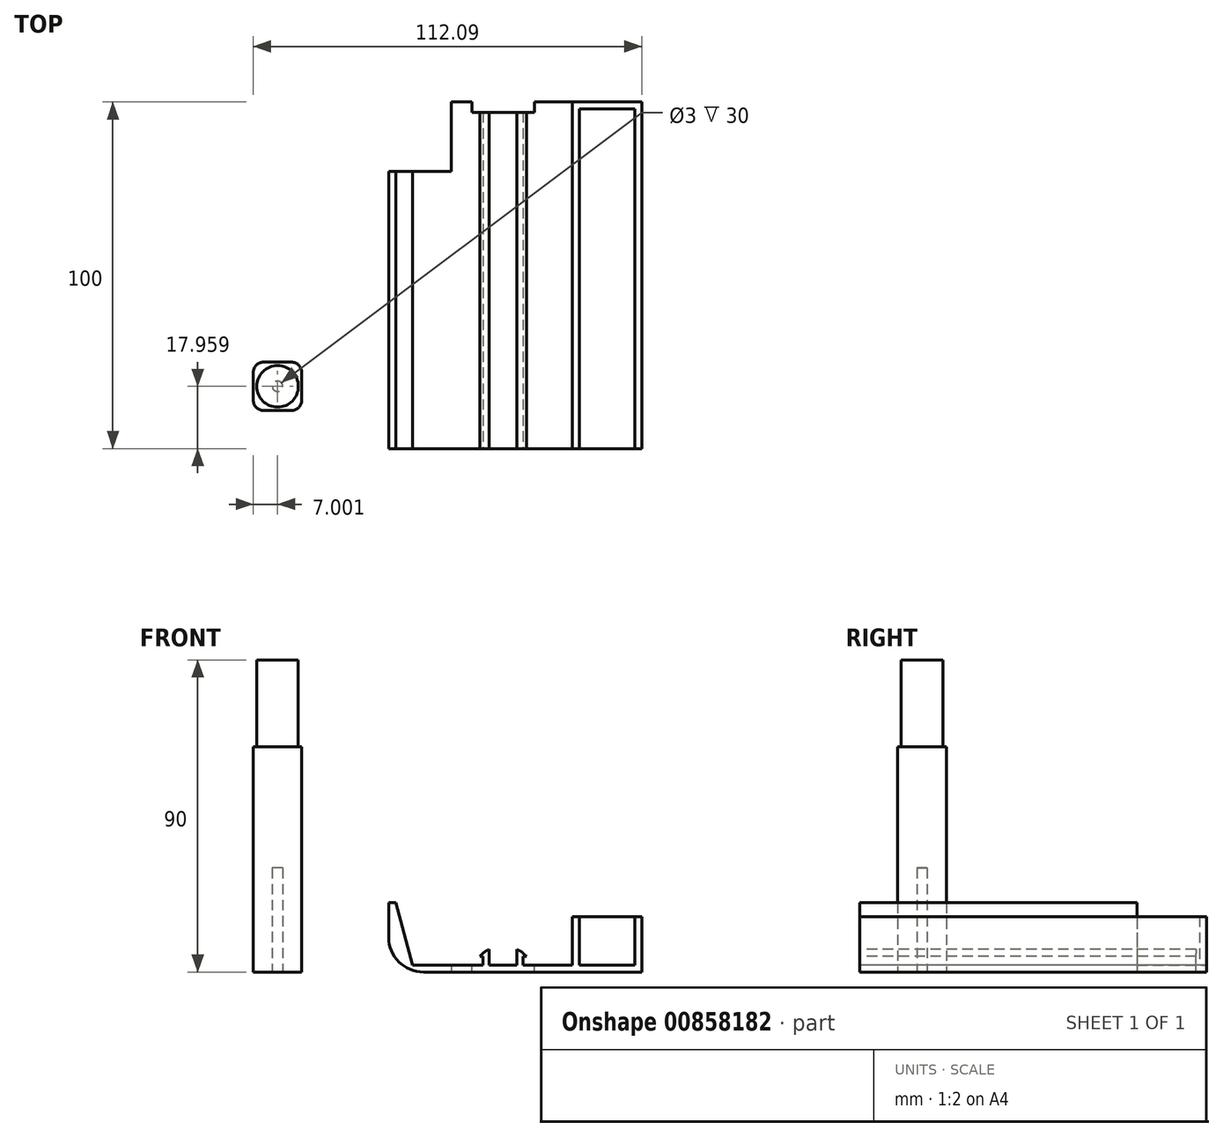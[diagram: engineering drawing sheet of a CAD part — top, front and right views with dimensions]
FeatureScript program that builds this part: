
annotation { "Feature Type Name" : "Feature", "Feature Type Description" : "" }
export const myFeature = defineFeature(function(context is Context, id is Id, definition is map)
    precondition{}
    {
        {
            var Q0;
            Q0=qCreatedBy(makeId("Top.planeOp"),FACE);
            var sketch = newSketch(context, id + "F0", { "sketchPlane" : qUnion([Q0])});
            skLineSegment(sketch, "E0.bottom", {"start": v(0, 0) * mm, "end": v(55, 0) * mm});
            skLineSegment(sketch, "E0.top", {"start": v(0, 100) * mm, "end": v(55, 100) * mm});
            skLineSegment(sketch, "E0.left", {"start": v(0, 0) * mm, "end": v(0, 100) * mm});
            skLineSegment(sketch, "E0.right", {"start": v(55, 0) * mm, "end": v(55, 100) * mm});
            skSolve(sketch);
        }
        {
            var Q0;
            Q0 = qSketchRegion(id + "F0", true);
            var Q1;
            Q1=makeQuery(id+"F0.imprint","IMPRINT",FACE,{"disambiguationData":[TD([[makeQuery(id+"F0.imprint","IMPRINT",EDGE,{"derivedFrom":sQuery(id+"F0.wireOp",EDGE,"E0.bottom")}),1.0]])]});
            extrude(context, id + "F1", {"entities" : qUnion([Q0, Q1]), "depth" : 2 * mm, "offsetDistance" : 25 * mm});
        }
        {
            var Q0;
            Q0=makeQuery(id+"F1.opExtrude","CAP_FACE",FACE,{"disambiguationData":[OSD([sQuery(id+"F0.wireOp",EDGE,"E0.bottom"),sQuery(id+"F0.wireOp",EDGE,"E0.top"),sQuery(id+"F0.wireOp",EDGE,"E0.left"),sQuery(id+"F0.wireOp",EDGE,"E0.right")])],"isStart":false});
            var sketch = newSketch(context, id + "F2", { "sketchPlane" : qUnion([Q0])});
            skLineSegment(sketch, "E1.bottom", {"start": v(55, 100) * mm, "end": v(53, 100) * mm});
            skLineSegment(sketch, "E1.top", {"start": v(55, 0) * mm, "end": v(53, 0) * mm});
            skLineSegment(sketch, "E1.left", {"start": v(55, 100) * mm, "end": v(55, 0) * mm});
            skLineSegment(sketch, "E1.right", {"start": v(53, 100) * mm, "end": v(53, 0) * mm});
            skLineSegment(sketch, "E2.bottom", {"start": v(35, 100) * mm, "end": v(37, 100) * mm});
            skLineSegment(sketch, "E2.top", {"start": v(35, 0) * mm, "end": v(37, 0) * mm});
            skLineSegment(sketch, "E2.left", {"start": v(35, 100) * mm, "end": v(35, 0) * mm});
            skLineSegment(sketch, "E2.right", {"start": v(37, 100) * mm, "end": v(37, 0) * mm});
            skLineSegment(sketch, "E3.bottom", {"start": v(37, 100) * mm, "end": v(53, 100) * mm});
            skLineSegment(sketch, "E3.top", {"start": v(37, 98) * mm, "end": v(53, 98) * mm});
            skLineSegment(sketch, "E3.left", {"start": v(37, 100) * mm, "end": v(37, 98) * mm});
            skLineSegment(sketch, "E3.right", {"start": v(53, 100) * mm, "end": v(53, 98) * mm});
            skSolve(sketch);
        }
        {
            var Q0;
            Q0=makeQuery(id+"F2.imprint","IMPRINT",FACE,{"disambiguationData":[TD([[makeQuery(id+"F2.imprint","IMPRINT",EDGE,{"derivedFrom":sQuery(id+"F2.wireOp",EDGE,"E2.bottom")}),-1.0]])]});
            var Q1;
            Q1=makeQuery(id+"F2.imprint","IMPRINT",FACE,{"disambiguationData":[TD([[makeQuery(id+"F2.imprint","IMPRINT",EDGE,{"derivedFrom":sQuery(id+"F2.wireOp",EDGE,"E1.bottom")}),-1.0]])]});
            var Q2;
            Q2=makeQuery(id+"F2.imprint","IMPRINT",FACE,{"disambiguationData":[TD([[makeQuery(id+"F2.imprint","IMPRINT",EDGE,{"derivedFrom":sQuery(id+"F2.wireOp",EDGE,"E3.bottom")}),-1.0]])]});
            extrude(context, id + "F3", {"entities" : qUnion([Q0, Q1, Q2]), "operationType" : NewBodyOperationType.ADD, "depth" : 14 * mm, "offsetDistance" : 25 * mm});
        }
        {
            var Q0;
            {var subQ0=sQuery(id+"F0.wireOp",EDGE,"E0.left");var subQ1=sQuery(id+"F0.wireOp",EDGE,"E0.top");var subQ2=sQuery(id+"F0.wireOp",EDGE,"E0.bottom");Q0=makeQuery(id+"F3.boolean.opBoolean","SPLIT",FACE,{"disambiguationData":[TD([makeQuery(id+"F1.opExtrude","SWEPT_FACE",FACE,{"disambiguationData":[OSD([subQ0])]})])],"derivedFrom":makeQuery(id+"F1.opExtrude","CAP_FACE",FACE,{"disambiguationData":[OSD([subQ2,subQ1,subQ0,sQuery(id+"F0.wireOp",EDGE,"E0.right")])],"isStart":false})});}
            var sketch = newSketch(context, id + "F4", { "sketchPlane" : qUnion([Q0])});
            skLineSegment(sketch, "E4.bottom", {"start": v(9.2, 100) * mm, "end": v(11, 100) * mm});
            skLineSegment(sketch, "E4.top", {"start": v(9.2, 0) * mm, "end": v(11, 0) * mm});
            skLineSegment(sketch, "E4.left", {"start": v(9.2, 100) * mm, "end": v(9.2, 0) * mm});
            skLineSegment(sketch, "E4.right", {"start": v(11, 100) * mm, "end": v(11, 0) * mm});
            skLineSegment(sketch, "E5.bottom", {"start": v(19, 100) * mm, "end": v(20.8, 100) * mm});
            skLineSegment(sketch, "E5.top", {"start": v(19, 0) * mm, "end": v(20.8, 0) * mm});
            skLineSegment(sketch, "E5.left", {"start": v(19, 100) * mm, "end": v(19, 0) * mm});
            skLineSegment(sketch, "E5.right", {"start": v(20.8, 100) * mm, "end": v(20.8, 0) * mm});
            skSolve(sketch);
        }
        {
            var Q0;
            Q0=makeQuery(id+"F4.imprint","IMPRINT",FACE,{"disambiguationData":[TD([[makeQuery(id+"F4.imprint","IMPRINT",EDGE,{"derivedFrom":sQuery(id+"F4.wireOp",EDGE,"E4.bottom")}),-1.0]])]});
            var Q1;
            Q1=makeQuery(id+"F4.imprint","IMPRINT",FACE,{"disambiguationData":[TD([[makeQuery(id+"F4.imprint","IMPRINT",EDGE,{"derivedFrom":sQuery(id+"F4.wireOp",EDGE,"E5.bottom")}),-1.0]])]});
            extrude(context, id + "F5", {"entities" : qUnion([Q0, Q1]), "operationType" : NewBodyOperationType.ADD, "depth" : 2.5 * mm, "offsetDistance" : 25 * mm});
        }
        {
            var Q0;
            Q0=makeQuery(id+"F5.opExtrude","CAP_FACE",FACE,{"disambiguationData":[OSD([sQuery(id+"F4.wireOp",EDGE,"E4.bottom"),sQuery(id+"F4.wireOp",EDGE,"E4.top"),sQuery(id+"F4.wireOp",EDGE,"E4.left"),sQuery(id+"F4.wireOp",EDGE,"E4.right")])],"isStart":false});
            var sketch = newSketch(context, id + "F6", { "sketchPlane" : qUnion([Q0])});
            skLineSegment(sketch, "E6.bottom", {"start": v(11, 0) * mm, "end": v(8.3, 0) * mm});
            skLineSegment(sketch, "E6.top", {"start": v(11, 100) * mm, "end": v(8.3, 100) * mm});
            skLineSegment(sketch, "E6.left", {"start": v(11, 0) * mm, "end": v(11, 100) * mm});
            skLineSegment(sketch, "E6.right", {"start": v(8.3, 0) * mm, "end": v(8.3, 100) * mm});
            skSolve(sketch);
        }
        {
            var Q0;
            Q0=makeQuery(id+"F5.opExtrude","CAP_FACE",FACE,{"disambiguationData":[OSD([sQuery(id+"F4.wireOp",EDGE,"E5.bottom"),sQuery(id+"F4.wireOp",EDGE,"E5.top"),sQuery(id+"F4.wireOp",EDGE,"E5.left"),sQuery(id+"F4.wireOp",EDGE,"E5.right")])],"isStart":false});
            var sketch = newSketch(context, id + "F7", { "sketchPlane" : qUnion([Q0])});
            skLineSegment(sketch, "E7.bottom", {"start": v(19, 100) * mm, "end": v(21.7, 100) * mm});
            skLineSegment(sketch, "E7.top", {"start": v(19, 0) * mm, "end": v(21.7, 0) * mm});
            skLineSegment(sketch, "E7.left", {"start": v(19, 100) * mm, "end": v(19, 0) * mm});
            skLineSegment(sketch, "E7.right", {"start": v(21.7, 100) * mm, "end": v(21.7, 0) * mm});
            skSolve(sketch);
        }
        {
            var Q0;
            {var subQ0=sQuery(id+"F7.wireOp",EDGE,"E7.left");Q0=makeQuery(id+"F7.imprint","IMPRINT",FACE,{"disambiguationData":[TD([[makeQuery(id+"F7.imprint","IMPRINT",EDGE,{"derivedFrom":subQ0}),1.0]])]});}
            var Q1;
            {var subQ2=sQuery(id+"F7.wireOp",EDGE,"E7.right");Q1=makeQuery(id+"F7.imprint","IMPRINT",FACE,{"disambiguationData":[TD([[makeQuery(id+"F7.imprint","IMPRINT",EDGE,{"derivedFrom":subQ2}),-1.0]])]});}
            var Q2;
            {var subQ2=sQuery(id+"F6.wireOp",EDGE,"E6.left");Q2=makeQuery(id+"F6.imprint","IMPRINT",FACE,{"disambiguationData":[TD([[makeQuery(id+"F6.imprint","IMPRINT",EDGE,{"derivedFrom":subQ2}),-1.0]])]});}
            var Q3;
            {var subQ2=sQuery(id+"F6.wireOp",EDGE,"E6.right");Q3=makeQuery(id+"F6.imprint","IMPRINT",FACE,{"disambiguationData":[TD([[makeQuery(id+"F6.imprint","IMPRINT",EDGE,{"derivedFrom":subQ2}),-1.0]])]});}
            extrude(context, id + "F8", {"entities" : qUnion([Q0, Q1, Q2, Q3]), "operationType" : NewBodyOperationType.ADD, "depth" : 2 * mm, "offsetDistance" : 25 * mm});
        }
        {
            var Q0;
            Q0=makeQuery(id+"F8.opExtrude","CAP_EDGE",EDGE,{"disambiguationData":[OSD([sQuery(id+"F6.wireOp",EDGE,"E6.right")])],"isStart":false});
            var Q1;
            Q1=makeQuery(id+"F8.opExtrude","CAP_EDGE",EDGE,{"disambiguationData":[OSD([sQuery(id+"F7.wireOp",EDGE,"E7.right")])],"isStart":false});
            chamfer(context, id + "F9", {"entities" : qUnion([Q0, Q1]), "width" : 2 * mm, "tangentPropagation" : true});
        }
        {
            var Q0;
            {var subQ0=sQuery(id+"F6.wireOp",EDGE,"E6.right");Q0=makeQuery(id+"F9.opChamfer","BLEND_EDGE",EDGE,{"blendedFrom":[makeQuery(id+"F8.opExtrude","CAP_EDGE",EDGE,{"disambiguationData":[OSD([subQ0])],"isStart":false}),makeQuery(id+"F8.opExtrude","CAP_FACE",FACE,{"disambiguationData":[OSD([sQuery(id+"F6.wireOp",EDGE,"E6.bottom"),sQuery(id+"F6.wireOp",EDGE,"E6.top"),sQuery(id+"F6.wireOp",EDGE,"E6.left"),subQ0])],"isStart":false})],"blendedInto":[makeQuery(id+"F8.opExtrude","CAP_FACE",FACE,{"disambiguationData":[OSD([sQuery(id+"F6.wireOp",EDGE,"E6.bottom"),sQuery(id+"F6.wireOp",EDGE,"E6.top"),sQuery(id+"F6.wireOp",EDGE,"E6.left"),subQ0])],"isStart":false})]});}
            var Q1;
            {var subQ0=sQuery(id+"F7.wireOp",EDGE,"E7.right");Q1=makeQuery(id+"F9.opChamfer","BLEND_EDGE",EDGE,{"blendedFrom":[makeQuery(id+"F8.opExtrude","CAP_EDGE",EDGE,{"disambiguationData":[OSD([subQ0])],"isStart":false}),makeQuery(id+"F8.opExtrude","CAP_FACE",FACE,{"disambiguationData":[OSD([sQuery(id+"F7.wireOp",EDGE,"E7.bottom"),sQuery(id+"F7.wireOp",EDGE,"E7.top"),sQuery(id+"F7.wireOp",EDGE,"E7.left"),subQ0])],"isStart":false})],"blendedInto":[makeQuery(id+"F8.opExtrude","CAP_FACE",FACE,{"disambiguationData":[OSD([sQuery(id+"F7.wireOp",EDGE,"E7.bottom"),sQuery(id+"F7.wireOp",EDGE,"E7.top"),sQuery(id+"F7.wireOp",EDGE,"E7.left"),subQ0])],"isStart":false})]});}
            fillet(context, id + "F10", {"entities" : qUnion([Q0, Q1]), "radius" : 5 * mm, "tangentPropagation" : true, "allowEdgeOverflow" : false});
        }
        {
            var Q0;
            {var subQ2=sQuery(id+"F0.wireOp",EDGE,"E0.bottom");var subQ4=sQuery(id+"F0.wireOp",EDGE,"E0.top");var subQ8=sQuery(id+"F0.wireOp",EDGE,"E0.left");Q0=makeQuery(id+"F5.boolean.opBoolean","SPLIT",FACE,{"disambiguationData":[TD([makeQuery(id+"F5.opExtrude","SWEPT_FACE",FACE,{"disambiguationData":[OSD([sQuery(id+"F4.wireOp",EDGE,"E4.right")])]})])],"derivedFrom":makeQuery(id+"F3.boolean.opBoolean","SPLIT",FACE,{"disambiguationData":[TD([makeQuery(id+"F1.opExtrude","SWEPT_FACE",FACE,{"disambiguationData":[OSD([subQ8])]})])],"derivedFrom":makeQuery(id+"F1.opExtrude","CAP_FACE",FACE,{"disambiguationData":[OSD([subQ2,subQ4,subQ8,sQuery(id+"F0.wireOp",EDGE,"E0.right")])],"isStart":false})})});}
            var sketch = newSketch(context, id + "F11", { "sketchPlane" : qUnion([Q0])});
            skLineSegment(sketch, "E8.bottom", {"start": v(24, 100) * mm, "end": v(6, 100) * mm});
            skLineSegment(sketch, "E8.top", {"start": v(24, 97) * mm, "end": v(6, 97) * mm});
            skLineSegment(sketch, "E8.left", {"start": v(24, 100) * mm, "end": v(24, 97) * mm});
            skLineSegment(sketch, "E8.right", {"start": v(6, 100) * mm, "end": v(6, 97) * mm});
            skSolve(sketch);
        }
        {
            var Q0;
            {var subQ3=sQuery(id+"F11.wireOp",EDGE,"E8.right");Q0=makeQuery(id+"F11.imprint","IMPRINT",FACE,{"disambiguationData":[TD([[makeQuery(id+"F11.imprint","IMPRINT",EDGE,{"derivedFrom":subQ3}),1.0]])]});}
            var Q1;
            {var subQ0=sQuery(id+"F11.wireOp",EDGE,"E8.bottom");var subQ1=makeQuery(id+"F5.opExtrude","CAP_EDGE",EDGE,{"disambiguationData":[OSD([sQuery(id+"F4.wireOp",EDGE,"E4.right")])],"isStart":true});var subQ2=makeQuery(id+"F11.imprint","INTERSECT",VERTEX,{"derivedFrom":[subQ1,subQ0]});var subQ3=makeQuery(id+"F5.opExtrude","CAP_EDGE",EDGE,{"disambiguationData":[OSD([sQuery(id+"F4.wireOp",EDGE,"E5.left")])],"isStart":true});var subQ4=makeQuery(id+"F11.imprint","INTERSECT",VERTEX,{"derivedFrom":[subQ3,subQ0]});Q1=makeQuery(id+"F11.imprint","IMPRINT",FACE,{"disambiguationData":[TD([[makeQuery(id+"F11.imprint","IMPRINT",EDGE,{"disambiguationData":[TD([[subQ2,-1.0],[subQ4,1.0]])],"derivedFrom":subQ0}),-1.0]])]});}
            var Q2;
            {var subQ3=sQuery(id+"F11.wireOp",EDGE,"E8.left");Q2=makeQuery(id+"F11.imprint","IMPRINT",FACE,{"disambiguationData":[TD([[makeQuery(id+"F11.imprint","IMPRINT",EDGE,{"derivedFrom":subQ3}),-1.0]])]});}
            extrude(context, id + "F12", {"entities" : qUnion([Q0, Q1, Q2]), "operationType" : NewBodyOperationType.REMOVE, "endBound" : BoundingType.THROUGH_ALL, "oppositeDirection" : true, "depth" : 5 * mm, "offsetDistance" : 25 * mm, "hasSecondDirection" : true, "secondDirectionOppositeDirection" : true, "secondDirectionDepth" : -10 * mm});
        }
        {
            var Q0;
            Q0=qCreatedBy(makeId("Top.planeOp"),FACE);
            var sketch = newSketch(context, id + "F13", { "sketchPlane" : qUnion([Q0])});
            skLineSegment(sketch, "E9.bottom", {"start": v(-57.09, 24.96) * mm, "end": v(-43.09, 24.96) * mm});
            skLineSegment(sketch, "E9.top", {"start": v(-57.09, 10.96) * mm, "end": v(-43.09, 10.96) * mm});
            skLineSegment(sketch, "E9.left", {"start": v(-57.09, 24.96) * mm, "end": v(-57.09, 10.96) * mm});
            skLineSegment(sketch, "E9.right", {"start": v(-43.09, 24.96) * mm, "end": v(-43.09, 10.96) * mm});
            skSolve(sketch);
        }
        {
            var Q0;
            Q0=makeQuery(id+"F13.imprint","IMPRINT",FACE,{"disambiguationData":[TD([[makeQuery(id+"F13.imprint","IMPRINT",EDGE,{"derivedFrom":sQuery(id+"F13.wireOp",EDGE,"E9.bottom")}),-1.0]])]});
            var sketch = newSketch(context, id + "F14", { "sketchPlane" : qUnion([Q0])});
            skSolve(sketch);
        }
        {
            var Q0;
            Q0=makeQuery(id+"F13.imprint","IMPRINT",FACE,{"disambiguationData":[TD([[makeQuery(id+"F13.imprint","IMPRINT",EDGE,{"derivedFrom":sQuery(id+"F13.wireOp",EDGE,"E9.bottom")}),-1.0]])]});
            extrude(context, id + "F15", {"entities" : qUnion([Q0]), "depth" : 65 * mm, "offsetDistance" : 25 * mm});
        }
        {
            var Q0;
            Q0=makeQuery(id+"F15.opExtrude","CAP_FACE",FACE,{"disambiguationData":[OSD([sQuery(id+"F13.wireOp",EDGE,"E9.bottom"),sQuery(id+"F13.wireOp",EDGE,"E9.top"),sQuery(id+"F13.wireOp",EDGE,"E9.left"),sQuery(id+"F13.wireOp",EDGE,"E9.right")])],"isStart":false});
            var sketch = newSketch(context, id + "F16", { "sketchPlane" : qUnion([Q0])});
            skCircle(sketch, "E10", {"center": v(-50.09, 17.96) * mm, "radius": 6 * mm});
            skPoint(sketch, "E10.first.point", {"position": v(-50.09, 23.96) * mm});
            skPoint(sketch, "E10.second.point", {"position": v(-56.09, 17.96) * mm});
            skPoint(sketch, "E10.third.point", {"position": v(-44.09, 17.96) * mm});
            skSolve(sketch);
        }
        {
            var Q0;
            Q0=makeQuery(id+"F16.imprint","IMPRINT",FACE,{"disambiguationData":[TD([[makeQuery(id+"F16.imprint","IMPRINT",EDGE,{"derivedFrom":sQuery(id+"F16.wireOp",EDGE,"E10")}),1.0]])]});
            extrude(context, id + "F17", {"entities" : qUnion([Q0]), "operationType" : NewBodyOperationType.ADD, "depth" : 25 * mm, "offsetDistance" : 25 * mm});
        }
        {
            var Q0;
            Q0=makeQuery(id+"F15.opExtrude","SWEPT_EDGE",EDGE,{"disambiguationData":[OSD([sQuery(id+"F13.wireOp",EDGE,"E9.top"),sQuery(id+"F13.wireOp",EDGE,"E9.left")])]});
            var Q1;
            Q1=makeQuery(id+"F15.opExtrude","SWEPT_EDGE",EDGE,{"disambiguationData":[OSD([sQuery(id+"F13.wireOp",EDGE,"E9.top"),sQuery(id+"F13.wireOp",EDGE,"E9.right")])]});
            var Q2;
            Q2=makeQuery(id+"F15.opExtrude","SWEPT_EDGE",EDGE,{"disambiguationData":[OSD([sQuery(id+"F13.wireOp",EDGE,"E9.bottom"),sQuery(id+"F13.wireOp",EDGE,"E9.right")])]});
            var Q3;
            Q3=makeQuery(id+"F15.opExtrude","SWEPT_EDGE",EDGE,{"disambiguationData":[OSD([sQuery(id+"F13.wireOp",EDGE,"E9.bottom"),sQuery(id+"F13.wireOp",EDGE,"E9.left")])]});
            fillet(context, id + "F18", {"entities" : qUnion([Q0, Q1, Q2, Q3]), "radius" : 3 * mm, "tangentPropagation" : true, "allowEdgeOverflow" : false});
        }
        {
            var Q0;
            Q0=makeQuery(id+"F14.imprint","IMPRINT",FACE,{"disambiguationData":[TD([[makeQuery(id+"F14.imprint","IMPRINT",EDGE,{"derivedFrom":makeQuery(id+"F13.imprint","IMPRINT",EDGE,{"derivedFrom":sQuery(id+"F13.wireOp",EDGE,"E9.bottom")})}),-1.0]])]});
            var sketch = newSketch(context, id + "F19", { "sketchPlane" : qUnion([Q0])});
            skCircle(sketch, "E11", {"center": v(-50.09, 17.96) * mm, "radius": 1.5 * mm});
            skSolve(sketch);
        }
        {
            var Q0;
            Q0=makeQuery(id+"F19.imprint","IMPRINT",FACE,{"disambiguationData":[TD([[makeQuery(id+"F19.imprint","IMPRINT",EDGE,{"derivedFrom":sQuery(id+"F19.wireOp",EDGE,"E11")}),1.0]])]});
            extrude(context, id + "F20", {"entities" : qUnion([Q0]), "operationType" : NewBodyOperationType.REMOVE, "depth" : 30 * mm, "offsetDistance" : 25 * mm});
        }
        {
            var Q0;
            Q0=qCreatedBy(makeId("Top.planeOp"),FACE);
            var sketch = newSketch(context, id + "F21", { "sketchPlane" : qUnion([Q0])});
            skLineSegment(sketch, "E12.bottom", {"start": v(0, 0) * mm, "end": v(-18, 0) * mm});
            skLineSegment(sketch, "E12.top", {"start": v(0, 80) * mm, "end": v(-18, 80) * mm});
            skLineSegment(sketch, "E12.left", {"start": v(0, 0) * mm, "end": v(0, 80) * mm});
            skLineSegment(sketch, "E12.right", {"start": v(-18, 0) * mm, "end": v(-18, 80) * mm});
            skSolve(sketch);
        }
        {
            var Q0;
            Q0=makeQuery(id+"F21.imprint","IMPRINT",FACE,{"disambiguationData":[TD([[makeQuery(id+"F21.imprint","IMPRINT",EDGE,{"derivedFrom":sQuery(id+"F21.wireOp",EDGE,"E12.bottom")}),-1.0]])]});
            extrude(context, id + "F22", {"entities" : qUnion([Q0]), "operationType" : NewBodyOperationType.ADD, "depth" : 20 * mm, "offsetDistance" : 25 * mm});
        }
        {
            var Q0;
            Q0=makeQuery(id+"F22.opExtrude","CAP_EDGE",EDGE,{"disambiguationData":[OSD([sQuery(id+"F21.wireOp",EDGE,"E12.left")])],"isStart":false});
            chamfer(context, id + "F23", {"entities" : qUnion([Q0]), "chamferType" : ChamferType.OFFSET_ANGLE, "width" : 16 * mm, "oppositeDirection" : false, "angle" : 75 * degree, "tangentPropagation" : true});
        }
        {
            var Q0;
            Q0=makeQuery(id+"F22.opExtrude","CAP_EDGE",EDGE,{"disambiguationData":[OSD([sQuery(id+"F21.wireOp",EDGE,"E12.right")])],"isStart":true});
            fillet(context, id + "F24", {"entities" : qUnion([Q0]), "radius" : 10 * mm, "tangentPropagation" : true, "allowEdgeOverflow" : false});
        }
    });
